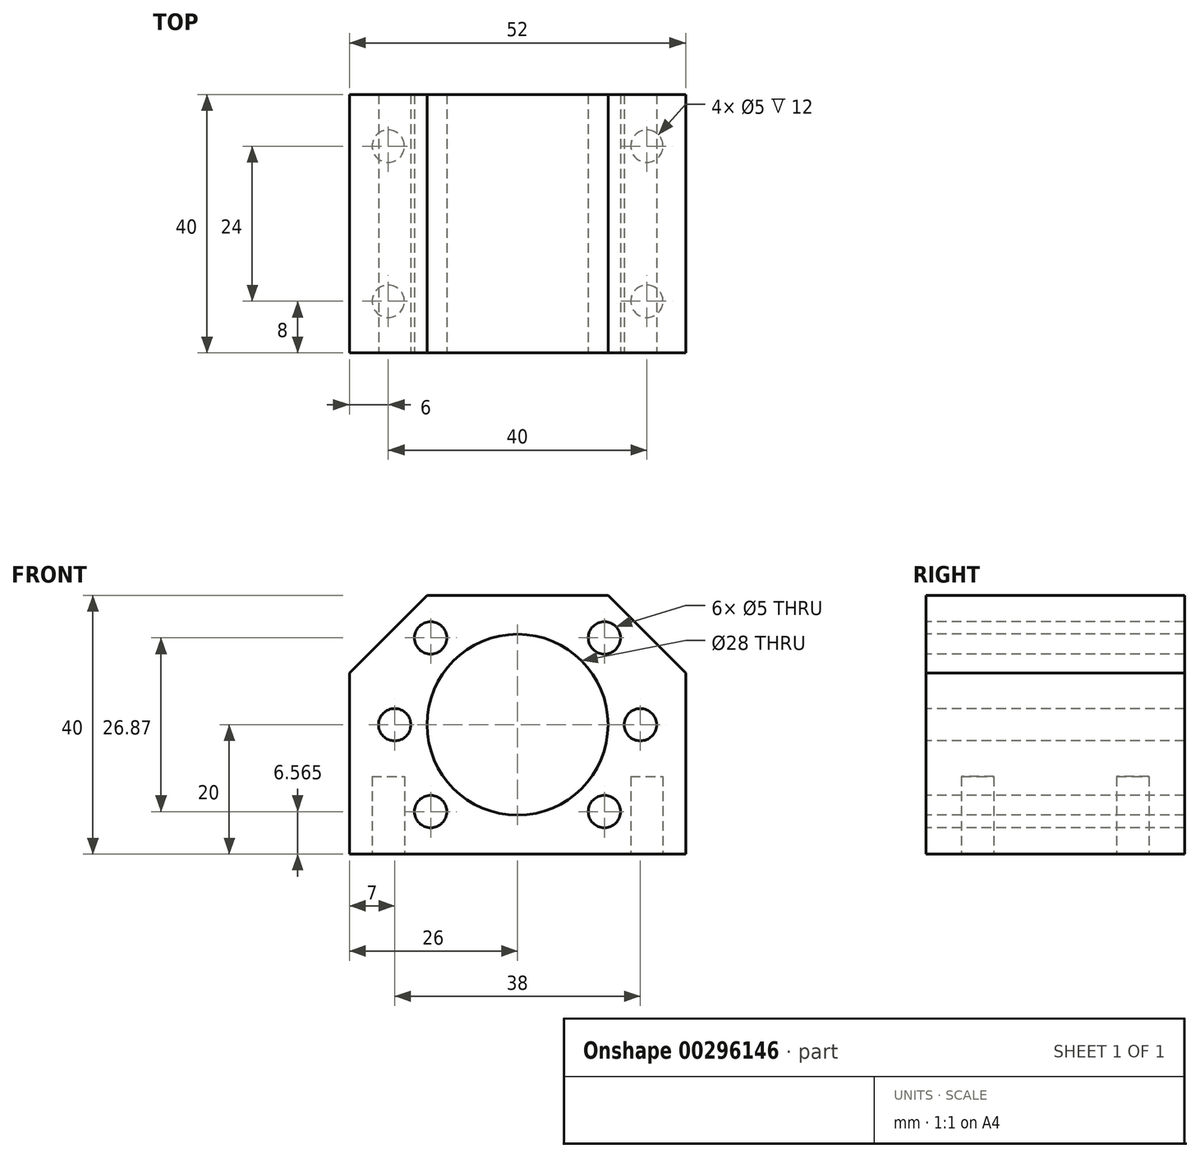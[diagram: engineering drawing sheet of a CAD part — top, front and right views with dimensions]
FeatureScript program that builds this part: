
annotation { "Feature Type Name" : "Feature", "Feature Type Description" : "" }
export const myFeature = defineFeature(function(context is Context, id is Id, definition is map)
    precondition{}
    {
        {
            var Q0;
            Q0=qCreatedBy(makeId("Front.planeOp"),FACE);
            var sketch = newSketch(context, id + "F0", { "sketchPlane" : qUnion([Q0])});
            skLineSegment(sketch, "E0.bottom", {"start": v(-14, 20) * mm, "end": v(14, 20) * mm});
            skLineSegment(sketch, "E0.top", {"start": v(-26, -20) * mm, "end": v(26, -20) * mm});
            skLineSegment(sketch, "E0.left", {"start": v(-26, 8) * mm, "end": v(-26, -20) * mm});
            skLineSegment(sketch, "E0.right", {"start": v(26, 8) * mm, "end": v(26, -20) * mm});
            skPoint(sketch, "E0.middle", {"position": v(0, 0) * mm});
            skLineSegment(sketch, "E1", {"start": v(-26, 8) * mm, "end": v(-14, 20) * mm});
            skLineSegment(sketch, "E2", {"start": v(14, 20) * mm, "end": v(26, 8) * mm});
            skPoint(sketch, "E3.orphan", {"position": v(-26, 20) * mm});
            skPoint(sketch, "E4.orphan", {"position": v(26, 20) * mm});
            skCircle(sketch, "E5", {"center": v(0, 0) * mm, "radius": 14 * mm});
            skCircle(sketch, "E6", {"center": v(0, 0) * mm, "radius": 19 * mm, "construction": true});
            skLineSegment(sketch, "E7", {"start": v(13.44, -13.44) * mm, "end": v(-42.02, 42.02) * mm, "construction": true});
            skLineSegment(sketch, "E8", {"start": v(-13.44, -13.44) * mm, "end": v(56.7, 56.7) * mm, "construction": true});
            skLineSegment(sketch, "E9", {"start": v(0, 20) * mm, "end": v(0, -20) * mm, "construction": true});
            skCircle(sketch, "E10", {"center": v(-13.44, 13.44) * mm, "radius": 2.5 * mm});
            skCircle(sketch, "E11", {"center": v(-13.44, -13.44) * mm, "radius": 2.5 * mm});
            skCircle(sketch, "E12", {"center": v(13.44, -13.44) * mm, "radius": 2.5 * mm});
            skCircle(sketch, "E13", {"center": v(13.44, 13.44) * mm, "radius": 2.5 * mm});
            skLineSegment(sketch, "E14", {"start": v(0, 0) * mm, "end": v(-26, 0) * mm, "construction": true});
            skLineSegment(sketch, "E15", {"start": v(-26, 0) * mm, "end": v(26, 0) * mm, "construction": true});
            skCircle(sketch, "E16", {"center": v(-19, 0) * mm, "radius": 2.5 * mm});
            skCircle(sketch, "E17", {"center": v(19, 0) * mm, "radius": 2.5 * mm});
            skSolve(sketch);
        }
        {
            var Q0;
            Q0=qSketchRegion(id+"F0",true);
            extrude(context, id + "F1", {"entities" : qUnion([Q0]), "oppositeDirection" : true, "depth" : 40 * mm, "offsetDistance" : 25 * mm});
        }
        {
            var Q0;
            Q0=makeQuery(id+"F1.opExtrude","SWEPT_FACE",FACE,{"disambiguationData":[OSD([sQuery(id+"F0.wireOp",EDGE,"E0.top")])]});
            var sketch = newSketch(context, id + "F2", { "sketchPlane" : qUnion([Q0])});
            skLineSegment(sketch, "E18.bottom", {"start": v(20, -32) * mm, "end": v(-20, -32) * mm, "construction": true});
            skLineSegment(sketch, "E18.top", {"start": v(20, -8) * mm, "end": v(-20, -8) * mm, "construction": true});
            skLineSegment(sketch, "E18.left", {"start": v(20, -32) * mm, "end": v(20, -8) * mm, "construction": true});
            skLineSegment(sketch, "E18.right", {"start": v(-20, -32) * mm, "end": v(-20, -8) * mm, "construction": true});
            skPoint(sketch, "E18.middle", {"position": v(0, -20) * mm});
            skCircle(sketch, "E19", {"center": v(20, -32) * mm, "radius": 2.5 * mm});
            skCircle(sketch, "E20", {"center": v(-20, -32) * mm, "radius": 2.5 * mm});
            skCircle(sketch, "E21", {"center": v(-20, -8) * mm, "radius": 2.5 * mm});
            skCircle(sketch, "E22", {"center": v(20, -8) * mm, "radius": 2.5 * mm});
            skSolve(sketch);
        }
        {
            var Q0;
            Q0 = qSketchRegion(id + "F2", true);
            extrude(context, id + "F3", {"entities" : qUnion([Q0]), "operationType" : NewBodyOperationType.REMOVE, "oppositeDirection" : true, "depth" : 12 * mm, "offsetDistance" : 25 * mm});
        }
    });
